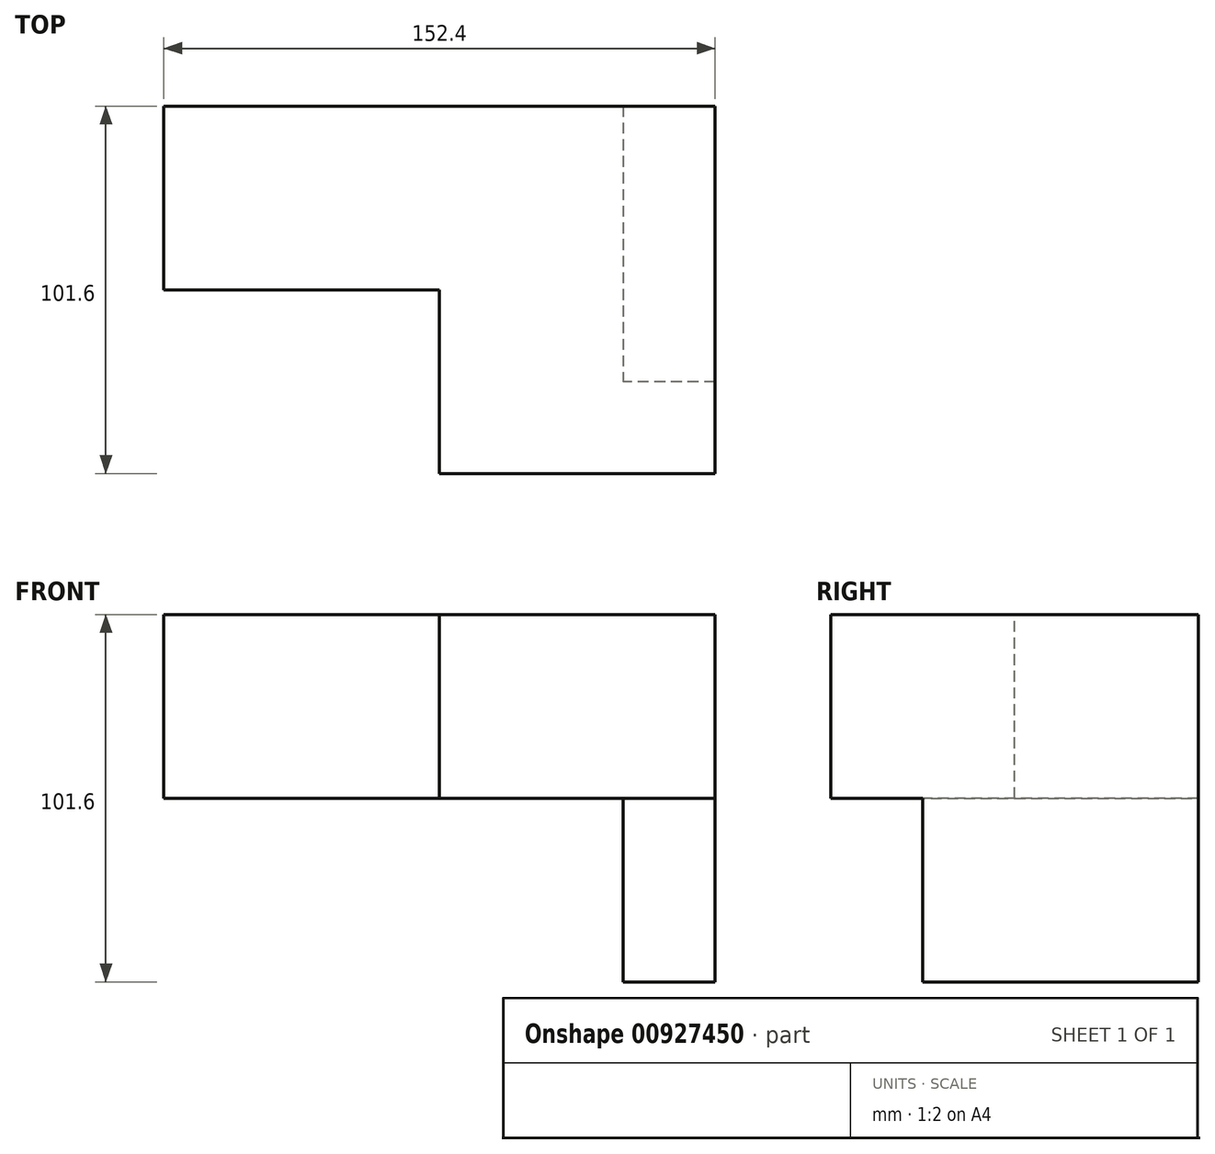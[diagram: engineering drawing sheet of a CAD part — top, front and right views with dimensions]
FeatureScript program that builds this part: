
annotation { "Feature Type Name" : "Feature", "Feature Type Description" : "" }
export const myFeature = defineFeature(function(context is Context, id is Id, definition is map)
    precondition{}
    {
        {
            var Q0;
            Q0=qCreatedBy(makeId("Right.planeOp"),FACE);
            var sketch = newSketch(context, id + "F0", { "sketchPlane" : qUnion([Q0])});
            skLineSegment(sketch, "E0.bottom", {"start": v(0, 0) * mm, "end": v(101.6, 0) * mm});
            skLineSegment(sketch, "E0.top", {"start": v(0, 50.8) * mm, "end": v(101.6, 50.8) * mm});
            skLineSegment(sketch, "E0.left", {"start": v(0, 0) * mm, "end": v(0, 50.8) * mm});
            skLineSegment(sketch, "E0.right", {"start": v(101.6, 0) * mm, "end": v(101.6, 50.8) * mm});
            skSolve(sketch);
        }
        {
            var Q0;
            Q0 = qSketchRegion(id + "F0", true);
            extrude(context, id + "F1", {"entities" : qUnion([Q0]), "depth" : 152.4 * mm, "offsetDistance" : 25.4 * mm});
        }
        {
            var Q0;
            Q0=qCreatedBy(makeId("Right.planeOp"),FACE);
            var sketch = newSketch(context, id + "F2", { "sketchPlane" : qUnion([Q0])});
            skLineSegment(sketch, "E1.bottom", {"start": v(0, 0) * mm, "end": v(50.8, 0) * mm});
            skLineSegment(sketch, "E1.top", {"start": v(0, 50.8) * mm, "end": v(50.8, 50.8) * mm});
            skLineSegment(sketch, "E1.left", {"start": v(0, 0) * mm, "end": v(0, 50.8) * mm});
            skLineSegment(sketch, "E1.right", {"start": v(50.8, 0) * mm, "end": v(50.8, 50.8) * mm});
            skSolve(sketch);
        }
        {
            var Q0;
            Q0 = qSketchRegion(id + "F2", true);
            extrude(context, id + "F3", {"entities" : qUnion([Q0]), "operationType" : NewBodyOperationType.REMOVE, "depth" : 76.2 * mm, "offsetDistance" : 25.4 * mm});
        }
        {
            var Q0;
            Q0=makeQuery(id+"F1.opExtrude","SWEPT_FACE",FACE,{"disambiguationData":[OSD([sQuery(id+"F0.wireOp",EDGE,"E0.bottom")])]});
            var sketch = newSketch(context, id + "F4", { "sketchPlane" : qUnion([Q0])});
            skLineSegment(sketch, "E2.bottom", {"start": v(152.4, -101.6) * mm, "end": v(127, -101.6) * mm});
            skLineSegment(sketch, "E2.top", {"start": v(152.4, -25.4) * mm, "end": v(127, -25.4) * mm});
            skLineSegment(sketch, "E2.left", {"start": v(152.4, -101.6) * mm, "end": v(152.4, -25.4) * mm});
            skLineSegment(sketch, "E2.right", {"start": v(127, -101.6) * mm, "end": v(127, -25.4) * mm});
            skSolve(sketch);
        }
        {
            var Q0;
            Q0 = qSketchRegion(id + "F4", true);
            extrude(context, id + "F5", {"entities" : qUnion([Q0]), "operationType" : NewBodyOperationType.ADD, "depth" : 50.8 * mm, "offsetDistance" : 25.4 * mm});
        }
    });
